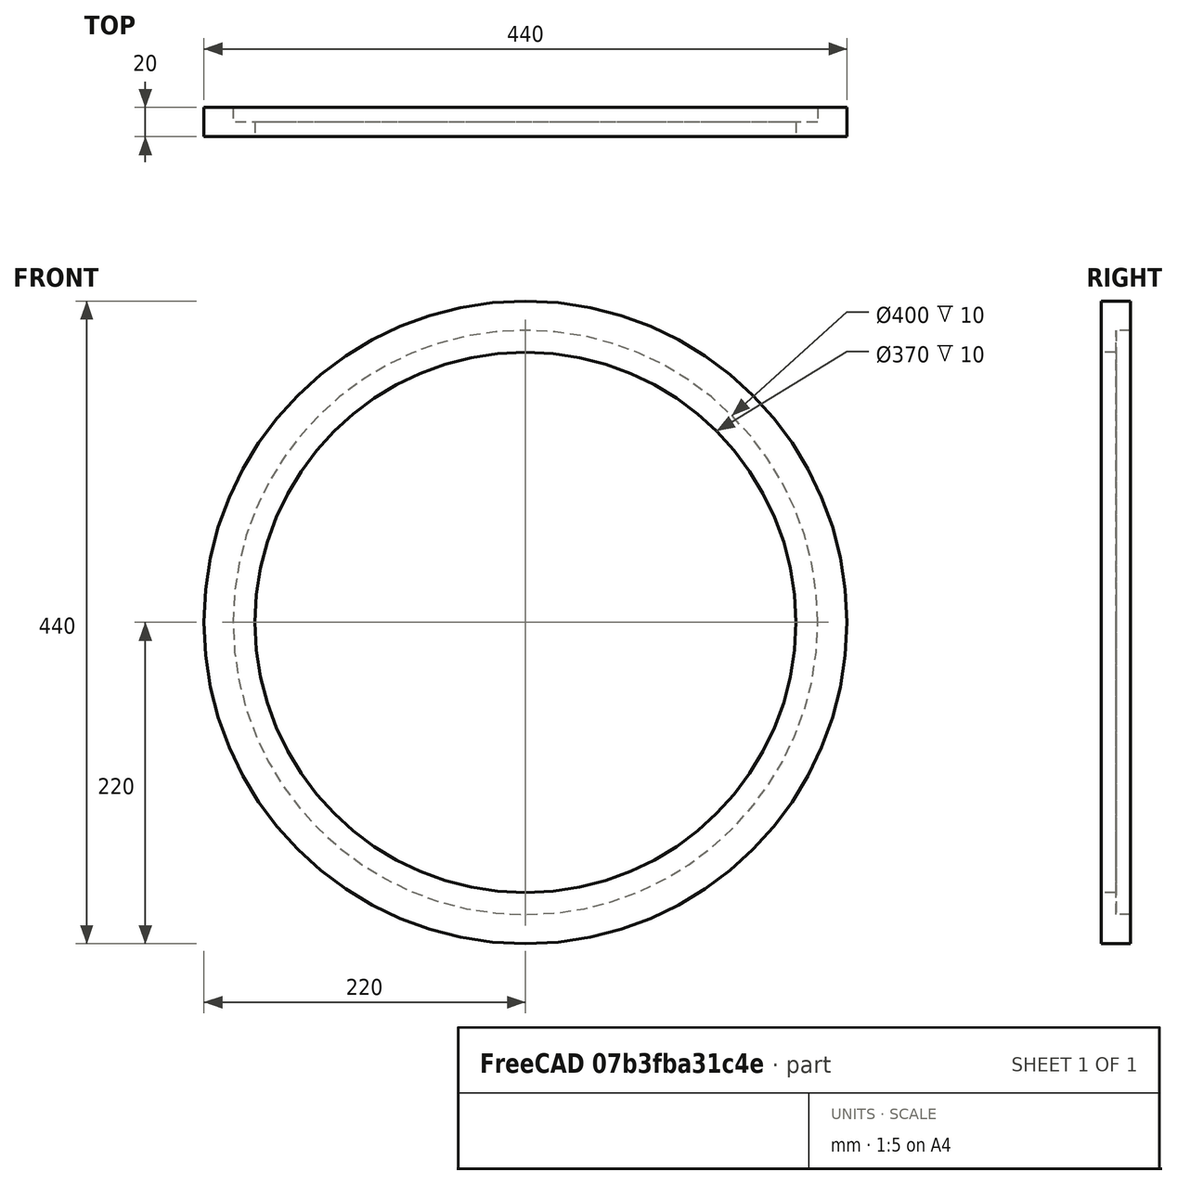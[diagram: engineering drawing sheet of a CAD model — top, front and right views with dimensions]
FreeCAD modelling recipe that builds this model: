
FCSTD DOCUMENT  (FreeCAD 0.18.4R)
Label: revolution_symm
License: All rights reserved
LicenseURL: http://en.wikipedia.org/wiki/All_rights_reserved
objects: TechDraw::DrawViewDimension×7, TechDraw::DrawViewPart×3, Spreadsheet::Sheet×1, TechDraw::DrawSVGTemplate×1, Sketcher::SketchObject×1, PartDesign::Revolution×1, PartDesign::Body×1, App::Part×1, Part::Feature×1, TechDraw::DrawPage×1
note: 5 computed .brp shape members not serialized (recipe doc carries the construction recipe); baked Part::Feature solids carry a one-line shape summary decoded from their .brp

FEATURE [Spreadsheet::Sheet] Spreadsheet  label="Parameters"
  cells = A1=r1; B1(r1)=185; A2=r2; B2(r2)=200; A3=r3; B3(r3)=220; A4=h1; B4(h1)=10; A5=h2; B5(h2)=20
FEATURE [TechDraw::DrawSVGTemplate] Template
  EditableTexts = Designed_by_Name=Ing. C. G. C. Romano; Drawing_number=Rotation symmetry views; FC-Date=2021-12-08; FC-SC=1:5; FC-SH=01; FC-Title=Ring mount; Subtitle=Optomechanics
  Height = 210
  Orientation = 1
  Width = 297
FEATURE [Sketcher::SketchObject] Sketch
  MapMode = 5
  Support = -> [XY_Plane001]
  expr: Constraints[16] = Parameters.h2
  expr: Constraints[15] = Parameters.h1
  expr: Constraints[12] = Parameters.r3
  expr: Constraints[11] = Parameters.r2
  expr: Constraints[10] = Parameters.r1
  sketch-geometry (6):
    g0: LineSegment StartX=185 StartY=0.440605 StartZ=0 EndX=220 EndY=0.440605 EndZ=0
    g1: LineSegment StartX=220 StartY=0.440605 StartZ=0 EndX=220 EndY=20.4406 EndZ=0
    g2: LineSegment StartX=220 StartY=20.4406 StartZ=0 EndX=200 EndY=20.4406 EndZ=0
    g3: LineSegment StartX=200 StartY=20.4406 StartZ=0 EndX=200 EndY=10.4406 EndZ=0
    g4: LineSegment StartX=200 StartY=10.4406 StartZ=0 EndX=185 EndY=10.4406 EndZ=0
    g5: LineSegment StartX=185 StartY=10.4406 StartZ=0 EndX=185 EndY=0.440605 EndZ=0
  constraints (17):
    c: Vertical(g5)
    c: Vertical(g1)
    c: Vertical(g3)
    c: Horizontal(g4)
    c: Horizontal(g0)
    c: Horizontal(g2)
    c: Coincident(g5,g4)
    c: Coincident(g3,g4)
    c: Coincident(g1,g2)
    c: Coincident(g2,g3)
    c: DistanceX(g-1,g0) = 185
    c: DistanceX(g-1,g3) = 200
    c: DistanceX(g-1,g1) = 220
    c: Coincident(g5,g0)
    c: Coincident(g0,g1)
    c: DistanceY(g5,g5) = 10
    c: DistanceY(g1,g1) = 20
FEATURE [PartDesign::Revolution] Revolution
  Angle = 360
  Axis = (0,1,0)
  Base = (0,0,0)
  Profile = -> Sketch
  ReferenceAxis = -> Sketch [V_Axis]
  Reversed = true
FEATURE [PartDesign::Body] Body
  Group = -> [Sketch,Revolution]
  Origin = -> Origin001
  Tip = -> Revolution
FEATURE [App::Part] Part
  Group = -> [Body]
  Origin = -> Origin
FEATURE [TechDraw::DrawViewPart] View
  CoarseView = false
  Direction = (0,1,0)
  Focus = 100
  HardHidden = false
  IsoCount = 0
  IsoHidden = false
  IsoVisible = false
  LockPosition = false
  Perspective = false
  Rotation = 0
  Scale = 0.2
  ScaleType = 0
  SeamHidden = false
  SeamVisible = false
  SmoothHidden = false
  SmoothVisible = false
  Source = -> [Body]
  X = 75.3942
  Y = 137.421
  expr: Scale = 0.2
FEATURE [TechDraw::DrawViewDimension] Dimension003
  Arbitrary = false
  FormatSpec = ⌀%.2f
  LockPosition = false
  MeasureType = 1
  OverTolerance = 0
  References2D = -> [View]
  Rotation = 0
  ScaleType = 0
  Type = 5
  UnderTolerance = 0
  X = -11.6496
  Y = -55.0292
FEATURE [TechDraw::DrawViewDimension] Dimension004
  Arbitrary = false
  FormatSpec = ⌀%.2f
  LockPosition = false
  MeasureType = 1
  OverTolerance = 0
  References2D = -> [View]
  Rotation = 0
  ScaleType = 0
  Type = 5
  UnderTolerance = 0
  X = 5.46715
  Y = -60.1387
FEATURE [TechDraw::DrawViewDimension] Dimension005
  Arbitrary = false
  FormatSpec = ⌀%.2f
  LockPosition = false
  MeasureType = 1
  OverTolerance = 0
  References2D = -> [View]
  Rotation = 0
  ScaleType = 0
  Type = 5
  UnderTolerance = 0
  X = 17.0657
  Y = -65.4015
FEATURE [Part::Feature] Body_cs
  shape: bbox 440 x 20 x 3e-07 mm, 0 faces, 0 solids (baked)
FEATURE [TechDraw::DrawViewPart] View001
  CoarseView = false
  Direction = (0,0,1)
  Focus = 100
  HardHidden = false
  IsoCount = 0
  IsoHidden = false
  IsoVisible = false
  LockPosition = false
  Perspective = false
  Rotation = 0
  Scale = 0.2
  ScaleType = 0
  SeamHidden = false
  SeamVisible = false
  SmoothHidden = false
  SmoothVisible = false
  Source = -> [Body_cs]
  X = 75.2163
  Y = 53.3885
  expr: Scale = 0.2
FEATURE [TechDraw::DrawViewDimension] Dimension
  Arbitrary = false
  FormatSpec = %.2f
  LockPosition = false
  MeasureType = 1
  OverTolerance = 0
  References2D = -> [View001]
  Rotation = 0
  ScaleType = 0
  Type = 1
  UnderTolerance = 0
  X = 56.9994
  Y = -6.08049
FEATURE [TechDraw::DrawViewDimension] Dimension006
  Arbitrary = false
  FormatSpec = %.2f
  LockPosition = false
  MeasureType = 1
  OverTolerance = 0
  References2D = -> [View001]
  Rotation = 0
  ScaleType = 0
  Type = 1
  UnderTolerance = 0
  X = 57.6123
  Y = 8.03204
FEATURE [TechDraw::DrawViewDimension] Dimension007
  Arbitrary = false
  FormatSpec = %.2f
  LockPosition = false
  MeasureType = 1
  OverTolerance = 0
  References2D = -> [View001]
  Rotation = 0
  ScaleType = 0
  Type = 2
  UnderTolerance = 0
  X = -49.5803
  Y = -18.6928
FEATURE [TechDraw::DrawViewDimension] Dimension008
  Arbitrary = false
  FormatSpec = %.2f
  LockPosition = false
  MeasureType = 1
  OverTolerance = 0
  References2D = -> [View001]
  Rotation = 0
  ScaleType = 0
  Type = 2
  UnderTolerance = 0
  X = -56.0641
  Y = -23.4185
FEATURE [TechDraw::DrawViewPart] View002
  CoarseView = false
  Direction = (-0.577,0.577,-0.577)
  Focus = 100
  HardHidden = false
  IsoCount = 0
  IsoHidden = false
  IsoVisible = false
  LockPosition = false
  Perspective = false
  Rotation = 0
  Scale = 0.2
  ScaleType = 0
  SeamHidden = false
  SeamVisible = false
  SmoothHidden = false
  SmoothVisible = false
  Source = -> [Part]
  X = 222.69
  Y = 139.029
  expr: Scale = 0.2
FEATURE [TechDraw::DrawPage] Page
  KeepUpdated = true
  ProjectionType = 1
  Template = -> Template
  Views = -> [View,Dimension003,Dimension004,Dimension005,View001,Dimension,Dimension006,Dimension007,Dimension008,View002]
